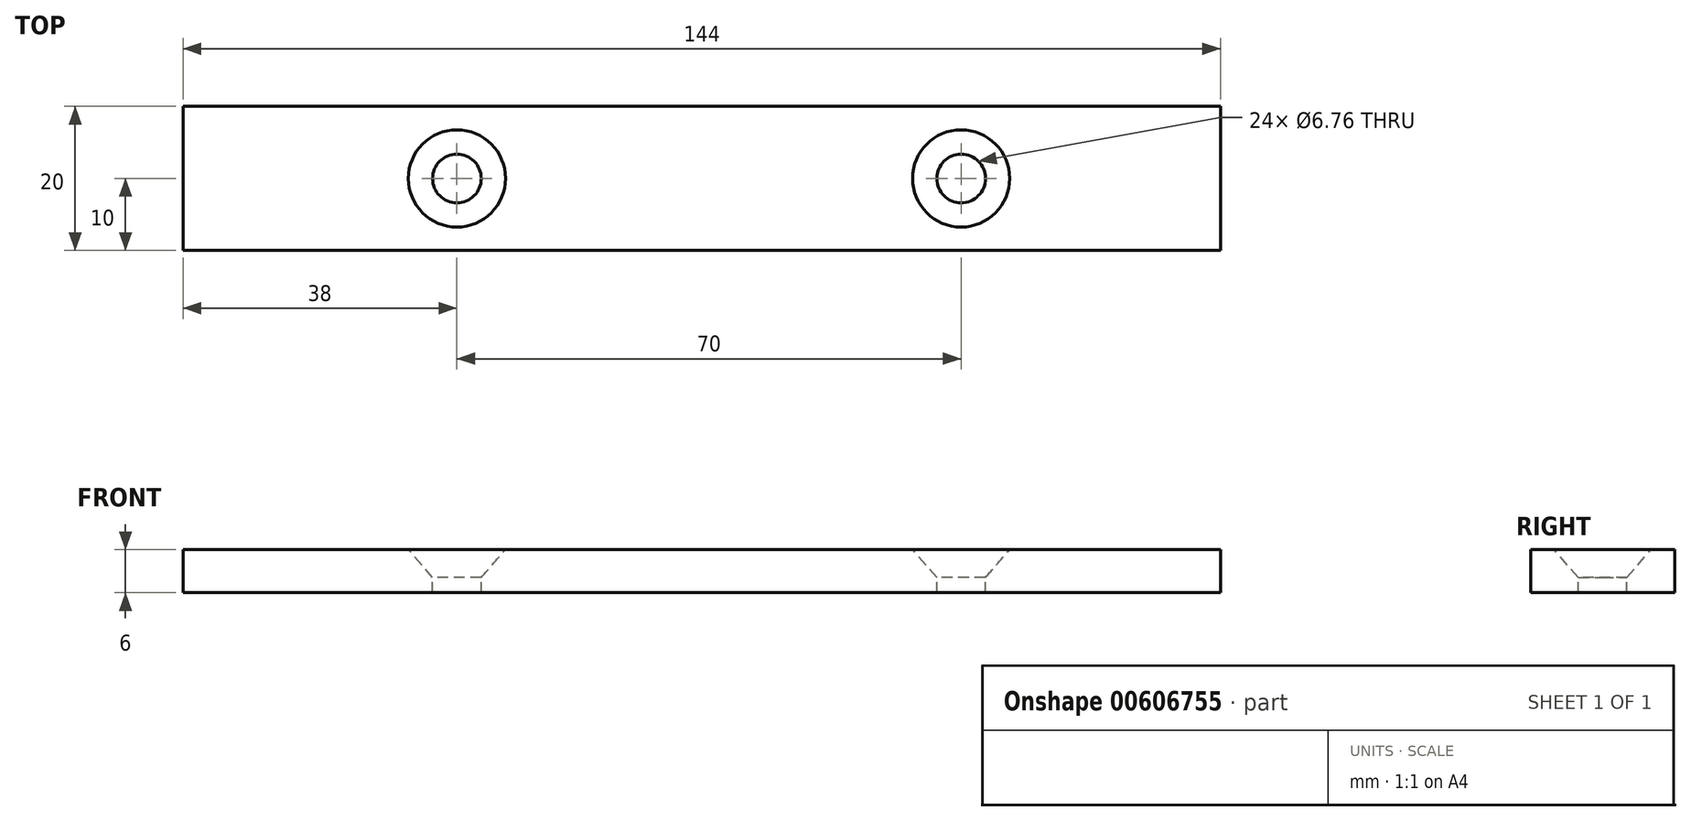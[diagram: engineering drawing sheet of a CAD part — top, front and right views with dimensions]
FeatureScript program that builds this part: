
annotation { "Feature Type Name" : "Feature", "Feature Type Description" : "" }
export const myFeature = defineFeature(function(context is Context, id is Id, definition is map)
    precondition{}
    {
        {
            var Q0;
            Q0=qCreatedBy(makeId("Top.planeOp"),FACE);
            var sketch = newSketch(context, id + "F0", { "sketchPlane" : qUnion([Q0])});
            skLineSegment(sketch, "E0.bottom", {"start": v(-72, 10) * mm, "end": v(72, 10) * mm});
            skLineSegment(sketch, "E0.top", {"start": v(-72, -10) * mm, "end": v(72, -10) * mm});
            skLineSegment(sketch, "E0.left", {"start": v(-72, 10) * mm, "end": v(-72, -10) * mm});
            skLineSegment(sketch, "E0.right", {"start": v(72, 10) * mm, "end": v(72, -10) * mm});
            skPoint(sketch, "E0.middle", {"position": v(0, 0) * mm});
            skSolve(sketch);
        }
        {
            var Q0;
            Q0 = qSketchRegion(id + "F0", true);
            extrude(context, id + "F1", {"entities" : qUnion([Q0]), "depth" : 6 * mm, "offsetDistance" : 25.4 * mm});
        }
        {
            var Q0;
            Q0=makeQuery(id+"F1.opExtrude","CAP_FACE",FACE,{"disambiguationData":[OSD([sQuery(id+"F0.wireOp",EDGE,"E0.bottom"),sQuery(id+"F0.wireOp",EDGE,"E0.top"),sQuery(id+"F0.wireOp",EDGE,"E0.left"),sQuery(id+"F0.wireOp",EDGE,"E0.right")])],"isStart":false});
            var sketch = newSketch(context, id + "F2", { "sketchPlane" : qUnion([Q0])});
            skPoint(sketch, "E1", {"position": v(36, 0) * mm});
            skPoint(sketch, "E2", {"position": v(-34, 0) * mm});
            skSolve(sketch);
        }
        {
            var Q0;
            Q0=sQuery(id+"F2.wireOp",VERTEX,"E2");
            var Q1;
            Q1=sQuery(id+"F2.wireOp",VERTEX,"E1");
            var Q2;
            Q2=makeQuery(id+"F1.opExtrude","SWEPT_BODY",BODY,{"disambiguationData":[OSD([sQuery(id+"F0.wireOp",EDGE,"E0.bottom"),sQuery(id+"F0.wireOp",EDGE,"E0.top"),sQuery(id+"F0.wireOp",EDGE,"E0.left"),sQuery(id+"F0.wireOp",EDGE,"E0.right")])]});
            hole(context, id + "F3", {"style" : HoleStyle.C_SINK, "endStyle" : HoleEndStyle.BLIND, "holeDiameter" : 6.76 * mm, "cSinkDiameter" : 13.5 * mm, "cSinkAngle" : 82 * degree, "majorDiameter" : 6.35 * mm, "holeDepth" : 16.51 * mm, "isTappedThrough" : true, "tappedDepth" : 12.7 * mm, "tapClearance" : 3, "startFromSketch" : true, "locations" : qUnion([Q0, Q1]), "scope" : qUnion([Q2])});
        }
    });
